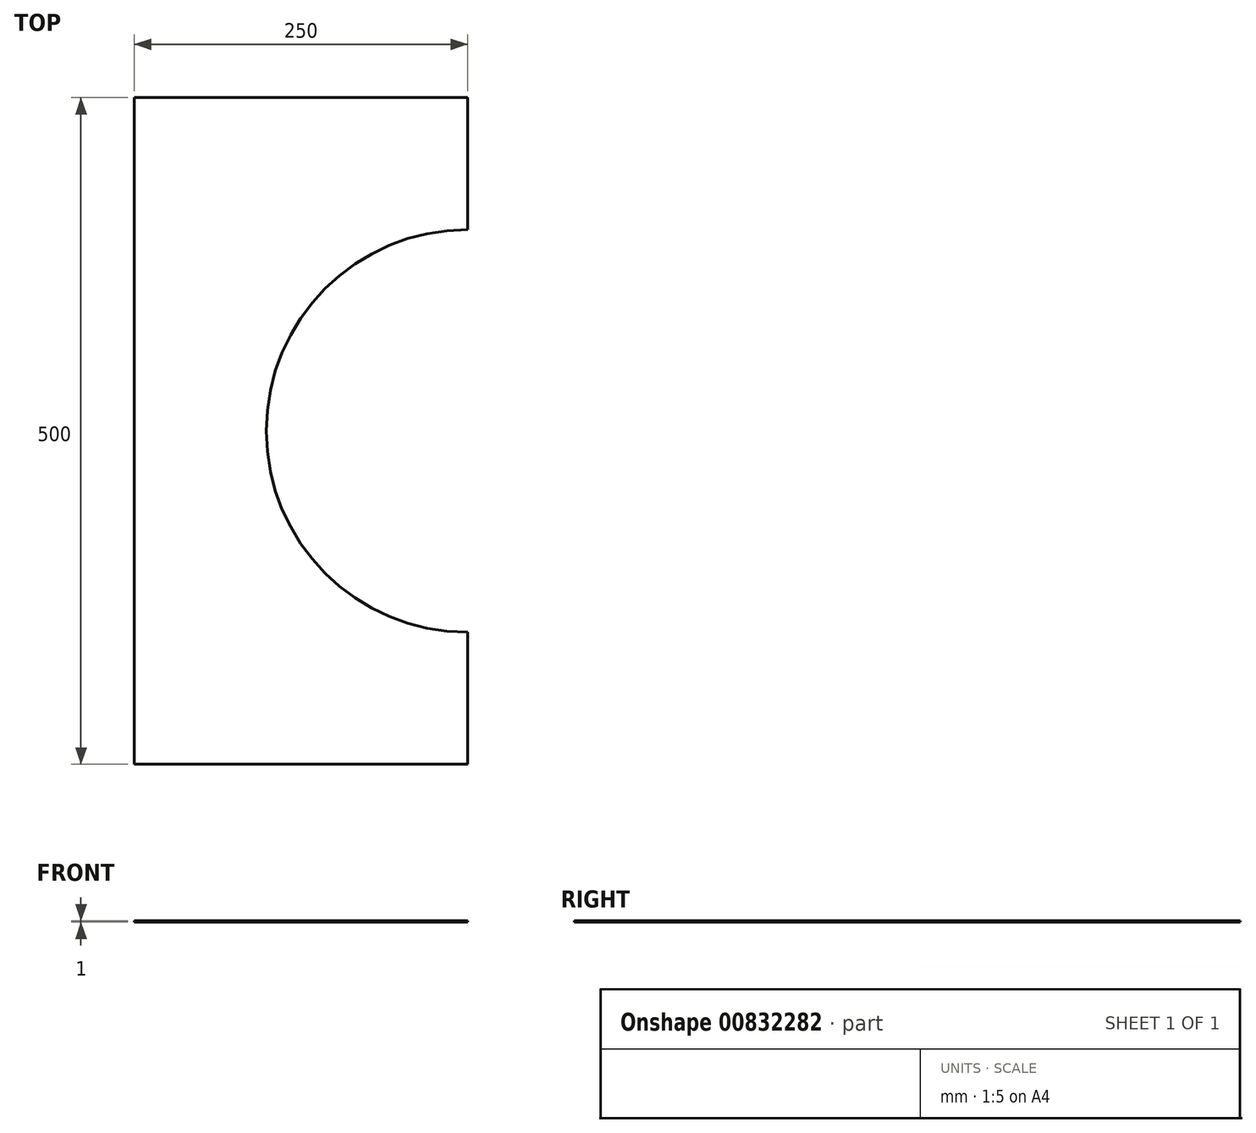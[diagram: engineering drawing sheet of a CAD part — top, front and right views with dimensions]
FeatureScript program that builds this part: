
annotation { "Feature Type Name" : "Feature", "Feature Type Description" : "" }
export const myFeature = defineFeature(function(context is Context, id is Id, definition is map)
    precondition{}
    {
        {
            var Q0;
            Q0=qCreatedBy(makeId("Top.planeOp"),FACE);
            var sketch = newSketch(context, id + "F0", { "sketchPlane" : qUnion([Q0])});
            skArc(sketch, "E0", {"start": v(0, 151) * mm, "mid": v(-151, 0) * mm, "end": v(0, -151) * mm});
            skLineSegment(sketch, "E1", {"start": v(0, -250) * mm, "end": v(0, -151) * mm});
            skLineSegment(sketch, "E2.trimOffspring", {"start": v(0, 151) * mm, "end": v(0, 250) * mm});
            skLineSegment(sketch, "E3", {"start": v(0, -250) * mm, "end": v(-250, -250) * mm});
            skLineSegment(sketch, "E4", {"start": v(-250, -250) * mm, "end": v(-250, 250) * mm});
            skLineSegment(sketch, "E5", {"start": v(-250, 250) * mm, "end": v(0, 250) * mm});
            skSolve(sketch);
        }
        {
            var Q0;
            Q0=makeQuery(id+"F0.imprint","IMPRINT",FACE,{"disambiguationData":[TD([[makeQuery(id+"F0.imprint","IMPRINT",EDGE,{"derivedFrom":sQuery(id+"F0.wireOp",EDGE,"E0")}),-1.0]])]});
            extrude(context, id + "F1", {"entities" : qUnion([Q0]), "depth" : 1 * mm, "offsetDistance" : 25 * mm});
        }
    });
